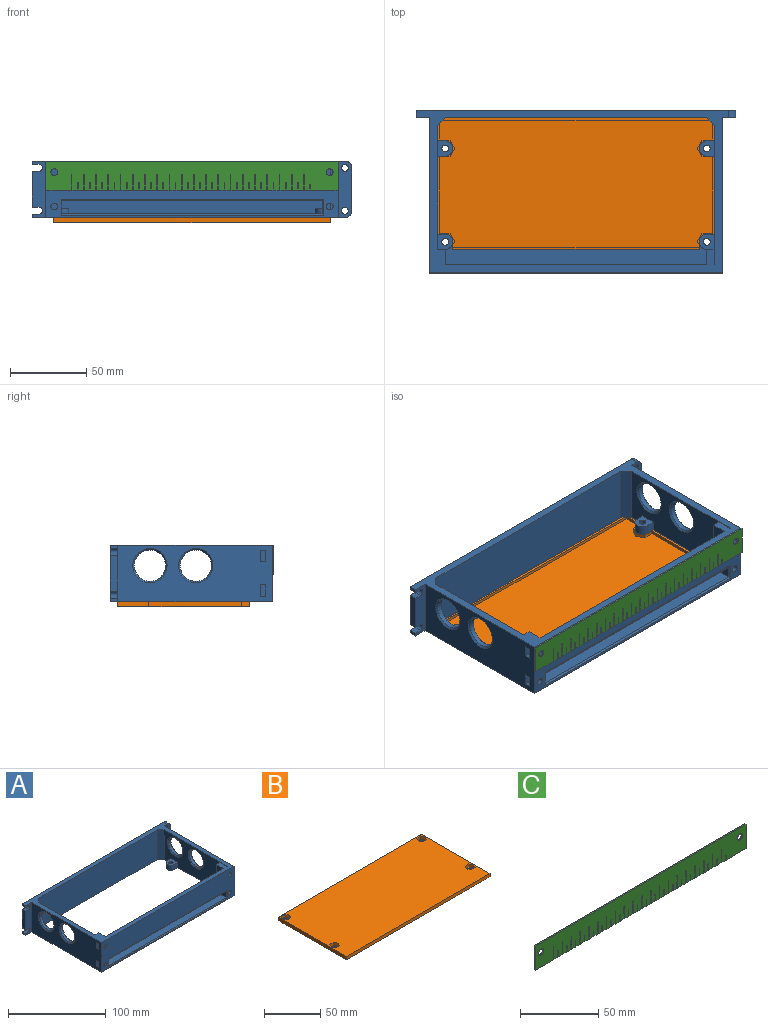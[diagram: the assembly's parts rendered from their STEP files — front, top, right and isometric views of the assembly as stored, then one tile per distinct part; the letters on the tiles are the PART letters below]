
ASSEMBLY  parts=3 mates=1
PART A: 147 faces, bbox 209x106x37 mm
  f0: cylinder r=1mm len=5mm, axis (0,-1,0), area 12.3mm2, adj f10,f16,f136,f145
  f1: plane 15.2x0.25mm, normal (0,1,0), area 3.8mm2, adj f11,f13,f123,f128
  f2: plane 1.1x0.25mm, normal (0,1,0), area 0.3mm2, adj f11,f13,f29,f129
  f3: cylinder r=2.25mm len=4.39mm, axis (0,-1,0), area 12.1mm2, adj f11,f71,f130
  f4: cylinder r=2.25mm len=4.5mm, axis (0,-1,0), area 63.6mm2, adj f10,f132
  f5: cylinder r=2.25mm len=4.39mm, axis (0,-1,0), area 12.1mm2, adj f11,f74,f124
  f6: cylinder r=2.25mm len=4.5mm, axis (0,-1,0), area 63.6mm2, adj f10,f125
  f7: plane 101x37mm, normal (-1,0,0), area 2890.7mm2, adj f9,f10,f23,f26,f108,f109,f110,f111
  f8: plane 171x37mm, normal (0,-1,0), area 6327mm2, adj f9,f26,f106,f107
  f9: plane 204.5x106mm, normal (0,0,-1), area 4958.2mm2, adj f7,f8,f10,f11,f14,f15,f18,f21
  f10: plane 191x37mm, normal (0,-1,0), area 5254mm2, adj f0,f4,f6,f7,f9,f14,f26,f27
  f11: plane 91x37mm, normal (-1,0,0), area 2361.4mm2, adj f1,f2,f3,f5,f9,f12,f26,f29
  f12: plane 3.6x0.25mm, normal (0,1,0), area 0.9mm2, adj f11,f13,f26,f122
  f13: plane 34.5x10mm, normal (1,0,0), area 283.3mm2, adj f1,f2,f12,f26,f29,f43,f57,f70
  f14: plane 101x37mm, normal (1,0,0), area 2890.7mm2, adj f9,f10,f18,f26,f122,f123,f124,f125
  f15: plane 81x37mm, normal (1,0,0), area 2077.8mm2, adj f9,f26,f33,f34,f35,f36,f38,f56
  f16: plane 170.5x26mm, normal (0,1,0), area 4432mm2, adj f0,f26,f27,f28,f30,f145
  f17: plane 170.5x18.99mm, normal (0,0,1), area 2397.7mm2, adj f22,f28,f30,f31,f44,f60,f62,f134
  f18: plane 37x9mm, normal (0,-1,0), area 292.5mm2, adj f9,f14,f24,f26,f51,f52,f64,f65
  f19: plane 23.5x5mm, normal (-1,0,0), area 117.5mm2, adj f21,f23,f50,f54
  f20: plane 5x2.25mm, normal (-1,0,0), area 11.2mm2, adj f21,f23,f26,f49
  f21: plane 209x37mm, normal (0,1,0), area 7636.1mm2, adj f9,f19,f20,f24,f25,f26,f48,f49
  f22: plane 161x2.5mm, normal (0,1,0), area 402.5mm2, adj f9,f17,f31,f44
  f23: plane 37x9mm, normal (0,-1,0), area 276.6mm2, adj f7,f9,f19,f20,f25,f26,f48,f49
  f24: plane 28x5mm, normal (1,0,0), area 140mm2, adj f18,f21,f64,f65
  f25: plane 5x2.25mm, normal (-1,0,0), area 11.3mm2, adj f9,f21,f23,f55
  f26: plane 204.5x106mm, normal (0,0,1), area 3065mm2, adj f7,f8,f10,f11,f12,f13,f14,f15
  f27: plane 170.5x5mm, normal (0,0,-1), area 852.5mm2, adj f10,f16,f28,f30,f146
  f28: plane 35.5x15mm, normal (1,0,0), area 388mm2, adj f10,f16,f17,f26,f27,f56,f60,f134
  f29: plane 10x0.25mm, normal (0,0,1), area 2.5mm2, adj f2,f11,f13,f43
  f30: plane 34.5x14mm, normal (-1,0,0), area 379mm2, adj f16,f17,f26,f27,f57,f62,f135
  f31: plane 6.2x5mm, normal (1,0,0), area 12.5mm2, adj f9,f17,f22,f34,f59,f60
  f32: cylinder r=2.25mm len=4.5mm, axis (0,0,-1), area 38.2mm2, adj f34,f98
  f33: plane 6.2x5mm, normal (0,1,0), area 31mm2, adj f9,f15,f34,f59
  f34: plane 10x10mm, normal (0,0,1), area 73.4mm2, adj f15,f31,f32,f33,f56,f59,f60
  f35: plane 6.2x5mm, normal (0,-1,0), area 31mm2, adj f9,f15,f38,f58
  f36: plane 6.2x5mm, normal (0,1,0), area 31mm2, adj f9,f15,f38,f58
  f37: cylinder r=2.25mm len=4.5mm, axis (0,0,-1), area 38.2mm2, adj f38,f91
  f38: plane 10x10mm, normal (0,0,1), area 73.4mm2, adj f15,f35,f36,f37,f58
  f39: plane 6.2x5mm, normal (0,1,0), area 31mm2, adj f9,f11,f42,f63
  f40: plane 6.2x5mm, normal (0,-1,0), area 31mm2, adj f9,f11,f42,f63
  f41: cylinder r=2.25mm len=4.5mm, axis (0,0,-1), area 38.2mm2, adj f42,f105
  f42: plane 10x10mm, normal (0,0,1), area 73.4mm2, adj f11,f39,f40,f41,f63
  f43: plane 3.7x0.25mm, normal (0,-1,0), area 0.9mm2, adj f11,f13,f29,f47
  f44: plane 6.2x5mm, normal (-1,0,0), area 12.5mm2, adj f9,f17,f22,f47,f61,f62
  f45: plane 6.2x5mm, normal (0,1,0), area 31mm2, adj f9,f11,f47,f61
  f46: cylinder r=2.25mm len=4.5mm, axis (0,0,-1), area 38.2mm2, adj f47,f84
  f47: plane 10x10mm, normal (0,0,1), area 73.4mm2, adj f11,f43,f44,f45,f46,f57,f61,f62
  f48: cylinder r=2.25mm len=5mm, axis (0,-1,0), area 35.3mm2, adj f21,f23,f49,f50
  f49: plane 5x4.5mm, normal (0,0,-1), area 22.5mm2, adj f20,f21,f23,f48
  f50: plane 5x4.5mm, normal (0,0,1), area 22.5mm2, adj f19,f21,f23,f48
  f51: cylinder r=2.25mm len=5mm, axis (0,-1,0), area 70.7mm2, adj f18,f21
  f52: cylinder r=2.25mm len=5mm, axis (0,-1,0), area 70.7mm2, adj f18,f21
  f53: cylinder r=2.25mm len=5mm, axis (0,-1,0), area 35.3mm2, adj f21,f23,f54,f55
  f54: plane 5x4.5mm, normal (0,0,-1), area 22.5mm2, adj f19,f21,f23,f53
  f55: plane 5x4.5mm, normal (0,0,1), area 22.5mm2, adj f21,f23,f25,f53
  f56: plane 30.8x5.25mm, normal (0,1,0), area 161.7mm2, adj f15,f26,f28,f34
  f57: plane 30.8x5mm, normal (0,1,0), area 154mm2, adj f13,f26,f30,f47
  f58: cylinder r=5mm len=10mm, axis (0,0,-1), area 97.4mm2, adj f9,f35,f36,f38
  f59: cylinder r=5mm len=6.2mm, axis (0,0,1), area 48.7mm2, adj f9,f31,f33,f34
  f60: cylinder r=5mm len=4.99mm, axis (0,0,1), area 28.1mm2, adj f17,f28,f31,f34
  f61: cylinder r=5mm len=6.2mm, axis (0,0,1), area 48.7mm2, adj f9,f44,f45,f47
  f62: cylinder r=5mm len=4.99mm, axis (0,0,1), area 28.1mm2, adj f17,f30,f44,f47
  f63: cylinder r=5mm len=10mm, axis (0,0,-1), area 97.4mm2, adj f9,f39,f40,f42
  f64: cylinder r=4.5mm len=5mm, axis (0,1,0), area 35.3mm2, adj f9,f18,f21,f24
  f65: cylinder r=4.5mm len=5mm, axis (0,-1,0), area 35.3mm2, adj f18,f21,f24,f26
  f66: cylinder r=10.25mm len=20.5mm, axis (1,0,0), area 193.2mm2, adj f142,f144
  f67: cylinder r=10.25mm len=20.5mm, axis (1,0,0), area 193.2mm2, adj f141,f143
  f68: cylinder r=10.25mm len=20.5mm, axis (1,0,0), area 193.2mm2, adj f137,f140
  f69: cylinder r=10.25mm len=20.5mm, axis (1,0,0), area 193.2mm2, adj f138,f139
  f70: cylinder r=2.25mm len=4.5mm, axis (0,-1,0), area 15.1mm2, adj f13,f72,f131
  f71: plane 4.39x1.75mm, normal (0,-1,0), area 5.7mm2, adj f3,f11
  f72: plane 4.5x2.5mm, normal (0,-1,0), area 9.1mm2, adj f13,f70
  f73: cylinder r=2.25mm len=4.5mm, axis (0,-1,0), area 15.1mm2, adj f13,f75,f126
  f74: plane 4.39x1.75mm, normal (0,-1,0), area 5.7mm2, adj f5,f11
  f75: plane 4.5x2.5mm, normal (0,-1,0), area 9.1mm2, adj f13,f73
  f76: cylinder r=2.25mm len=4.5mm, axis (0,-1,0), area 63.6mm2, adj f10,f118
  f77: cylinder r=2.25mm len=4.5mm, axis (0,-1,0), area 63.6mm2, adj f10,f109
  f78: plane 3.63x3.5mm, normal (-0.5,0.87,0), area 14.7mm2, adj f9,f79,f83,f84
  f79: plane 3.63x3.5mm, normal (0.5,0.87,0), area 14.7mm2, adj f9,f78,f80,f84
  f80: plane 4.19x3.5mm, normal (1,0,0), area 14.7mm2, adj f9,f79,f81,f84
  f81: plane 3.63x3.5mm, normal (0.5,-0.87,0), area 14.7mm2, adj f9,f80,f82,f84
  f82: plane 3.63x3.5mm, normal (-0.5,-0.87,0), area 14.7mm2, adj f9,f81,f83,f84
  f83: plane 4.19x3.5mm, normal (-1,0,0), area 14.7mm2, adj f9,f78,f82,f84
  f84: plane 8.37x7.25mm, normal (0,0,-1), area 29.6mm2, adj f46,f78,f79,f80,f81,f82,f83
  f85: plane 4.19x3.5mm, normal (0,-1,0), area 14.7mm2, adj f9,f86,f90,f91
  f86: plane 3.63x3.5mm, normal (-0.87,-0.5,0), area 14.7mm2, adj f9,f85,f87,f91
  f87: plane 3.63x3.5mm, normal (-0.87,0.5,0), area 14.7mm2, adj f9,f86,f88,f91
  f88: plane 4.19x3.5mm, normal (0,1,0), area 14.7mm2, adj f9,f87,f89,f91
  f89: plane 3.63x3.5mm, normal (0.87,0.5,0), area 14.7mm2, adj f9,f88,f90,f91
  f90: plane 3.63x3.5mm, normal (0.87,-0.5,0), area 14.7mm2, adj f9,f85,f89,f91
  f91: plane 8.37x7.25mm, normal (0,0,-1), area 29.6mm2, adj f37,f85,f86,f87,f88,f89,f90
  f92: plane 4.19x3.5mm, normal (0,-1,0), area 14.7mm2, adj f9,f93,f97,f98
  f93: plane 3.63x3.5mm, normal (-0.87,-0.5,0), area 14.7mm2, adj f9,f92,f94,f98
  f94: plane 3.63x3.5mm, normal (-0.87,0.5,0), area 14.7mm2, adj f9,f93,f95,f98
  f95: plane 4.19x3.5mm, normal (0,1,0), area 14.7mm2, adj f9,f94,f96,f98
  f96: plane 3.63x3.5mm, normal (0.87,0.5,0), area 14.7mm2, adj f9,f95,f97,f98
  f97: plane 3.63x3.5mm, normal (0.87,-0.5,0), area 14.7mm2, adj f9,f92,f96,f98
  f98: plane 8.37x7.25mm, normal (0,0,-1), area 29.6mm2, adj f32,f92,f93,f94,f95,f96,f97
  f99: plane 3.63x3.5mm, normal (-0.5,0.87,0), area 14.7mm2, adj f9,f100,f104,f105
  f100: plane 3.63x3.5mm, normal (0.5,0.87,0), area 14.7mm2, adj f9,f99,f101,f105
  f101: plane 4.19x3.5mm, normal (1,0,0), area 14.7mm2, adj f9,f100,f102,f105
  f102: plane 3.63x3.5mm, normal (0.5,-0.87,0), area 14.7mm2, adj f9,f101,f103,f105
  f103: plane 3.63x3.5mm, normal (-0.5,-0.87,0), area 14.7mm2, adj f9,f102,f104,f105
  f104: plane 4.19x3.5mm, normal (-1,0,0), area 14.7mm2, adj f9,f99,f103,f105
  f105: plane 8.37x7.25mm, normal (0,0,-1), area 29.6mm2, adj f41,f99,f100,f101,f102,f103,f104
  f106: plane 37x5mm, normal (0.71,-0.71,0), area 261.6mm2, adj f8,f9,f15,f26
  f107: plane 37x5mm, normal (-0.71,-0.71,0), area 261.6mm2, adj f8,f9,f11,f26
  f108: plane 9x7.3mm, normal (0,-1,0), area 49.8mm2, adj f7,f110,f111,f112,f114
  f109: plane 9x7.3mm, normal (0,1,0), area 49.8mm2, adj f7,f77,f110,f111,f112
  f110: plane 9x3.5mm, normal (0,0,-1), area 31.5mm2, adj f7,f108,f109,f112
  f111: plane 9x3.5mm, normal (0,0,1), area 31.5mm2, adj f7,f108,f109,f112
  f112: plane 7.3x3.5mm, normal (-1,0,0), area 25.6mm2, adj f108,f109,f110,f111
  f113: plane 4.5x4.5mm, normal (0,-1,0), area 15.9mm2, adj f114
  f114: cylinder r=2.25mm len=4.5mm, axis (0,-1,0), area 28.3mm2, adj f108,f113
  f115: plane 9x3.5mm, normal (0,0,-1), area 31.5mm2, adj f7,f116,f118,f119
  f116: plane 9x7.3mm, normal (0,-1,0), area 49.8mm2, adj f7,f115,f117,f119,f121
  f117: plane 9x3.5mm, normal (0,0,1), area 31.5mm2, adj f7,f116,f118,f119
  f118: plane 9x7.3mm, normal (0,1,0), area 49.8mm2, adj f7,f76,f115,f117,f119
  f119: plane 7.3x3.5mm, normal (-1,0,0), area 25.6mm2, adj f115,f116,f117,f118
  f120: plane 4.5x4.5mm, normal (0,-1,0), area 15.9mm2, adj f121
  f121: cylinder r=2.25mm len=4.5mm, axis (0,-1,0), area 28.3mm2, adj f116,f120
  f122: plane 9x3.5mm, normal (0,0,-1), area 30.8mm2, adj f11,f12,f13,f14,f124,f125,f126,f127
  f123: plane 9x3.5mm, normal (0,0,1), area 30.8mm2, adj f1,f11,f13,f14,f124,f125,f126,f127
  f124: plane 7.3x5mm, normal (0,-1,0), area 30.8mm2, adj f5,f11,f14,f122,f123
  f125: plane 9x7.3mm, normal (0,1,0), area 49.8mm2, adj f6,f14,f122,f123,f127
  f126: plane 7.3x3.75mm, normal (0,-1,0), area 18.3mm2, adj f13,f73,f122,f123,f127
  f127: plane 7.3x3.5mm, normal (1,0,0), area 25.6mm2, adj f122,f123,f125,f126
  f128: plane 9x3.5mm, normal (0,0,-1), area 30.8mm2, adj f1,f11,f13,f14,f130,f131,f132,f133
  f129: plane 9x3.5mm, normal (0,0,1), area 30.8mm2, adj f2,f11,f13,f14,f130,f131,f132,f133
  f130: plane 7.3x5mm, normal (0,-1,0), area 30.8mm2, adj f3,f11,f14,f128,f129
  f131: plane 7.3x3.75mm, normal (0,-1,0), area 18.3mm2, adj f13,f70,f128,f129,f133
  f132: plane 9x7.3mm, normal (0,1,0), area 49.8mm2, adj f4,f14,f128,f129,f133
  f133: plane 7.3x3.5mm, normal (1,0,0), area 25.6mm2, adj f128,f129,f131,f132
  f134: plane 171.5x1mm, normal (0,-0.71,0.71), area 241.8mm2, adj f10,f17,f28,f135
  f135: plane 10.5x1mm, normal (-0.71,-0.71,0), area 13.4mm2, adj f10,f30,f134,f136
  f136: plane 170.5x1mm, normal (0,-0.71,-0.71), area 167.8mm2, adj f0,f10,f135,f145,f146
  f137: cone r=11.25mm half-angle=45deg, axis (-1,0,0), area 95.5mm2, adj f11,f68
  f138: cone r=10.25mm half-angle=45deg, axis (-1,0,0), area 95.5mm2, adj f11,f69
  f139: cone r=11.25mm half-angle=45deg, axis (1,0,0), area 95.5mm2, adj f14,f69
  f140: cone r=10.25mm half-angle=45deg, axis (1,0,0), area 95.5mm2, adj f14,f68
  f141: cone r=11.25mm half-angle=45deg, axis (1,0,0), area 95.5mm2, adj f15,f67
  f142: cone r=10.25mm half-angle=45deg, axis (1,0,0), area 95.5mm2, adj f15,f66
  f143: cone r=10.25mm half-angle=45deg, axis (-1,0,0), area 95.5mm2, adj f7,f67
  f144: cone r=11.25mm half-angle=45deg, axis (-1,0,0), area 95.5mm2, adj f7,f66
  f145: plane 170.45x5mm, normal (0,0,1), area 127.5mm2, adj f0,f10,f16,f136,f146
  f146: plane 1x0.3mm, normal (1,0,0), area 0.3mm2, adj f10,f27,f136,f145
PART B: 73 faces, bbox 181x86x5 mm
  f0: plane 181x86mm, normal (0,0,-1), area 972mm2, adj f6,f7,f8,f9,f10,f12,f14,f16
  f1: plane 181x86mm, normal (0,0,1), area 15355.2mm2, adj f6,f7,f8,f9,f18,f19,f20,f21
  f2: cylinder r=2.25mm len=4.5mm, axis (0,0,1), area 25.4mm2, adj f11,f45
  f3: cylinder r=2.25mm len=4.5mm, axis (0,0,1), area 25.4mm2, adj f13,f38
  f4: cylinder r=2.25mm len=4.5mm, axis (0,0,1), area 25.4mm2, adj f15,f31
  f5: cylinder r=2.25mm len=4.5mm, axis (0,0,1), area 25.4mm2, adj f17,f24
  f6: plane 181x3.5mm, normal (0,-1,0), area 633.5mm2, adj f0,f1,f7,f9
  f7: plane 86x3.5mm, normal (1,0,0), area 301mm2, adj f0,f1,f6,f8
  f8: plane 181x3.5mm, normal (0,1,0), area 633.5mm2, adj f0,f1,f7,f9
  f9: plane 86x3.5mm, normal (-1,0,0), area 301mm2, adj f0,f1,f6,f8
  f10: cylinder r=3.4mm len=6.8mm, axis (0,0,1), area 32mm2, adj f0,f11
  f11: plane 6.8x6.8mm, normal (0,0,-1), area 20.4mm2, adj f2,f10
  f12: cylinder r=3.4mm len=6.8mm, axis (0,0,1), area 32mm2, adj f0,f13
  f13: plane 6.8x6.8mm, normal (0,0,-1), area 20.4mm2, adj f3,f12
  f14: cylinder r=3.4mm len=6.8mm, axis (0,0,1), area 32mm2, adj f0,f15
  f15: plane 6.8x6.8mm, normal (0,0,-1), area 20.4mm2, adj f4,f14
  f16: cylinder r=3.4mm len=6.8mm, axis (0,0,1), area 32mm2, adj f0,f17
  f17: plane 6.8x6.8mm, normal (0,0,-1), area 20.4mm2, adj f5,f16
  f18: plane 3.9x3.2mm, normal (0.87,-0.5,0), area 14.4mm2, adj f1,f19,f23,f24
  f19: plane 3.9x3.2mm, normal (0.87,0.5,0), area 14.4mm2, adj f1,f18,f20,f24
  f20: plane 4.5x3.2mm, normal (0,1,0), area 14.4mm2, adj f1,f19,f21,f24
  f21: plane 3.9x3.2mm, normal (-0.87,0.5,0), area 14.4mm2, adj f1,f20,f22,f24
  f22: plane 3.9x3.2mm, normal (-0.87,-0.5,0), area 14.4mm2, adj f1,f21,f23,f24
  f23: plane 4.5x3.2mm, normal (0,-1,0), area 14.4mm2, adj f1,f18,f22,f24
  f24: plane 9.01x7.8mm, normal (0,0,1), area 36.8mm2, adj f5,f18,f19,f20,f21,f22,f23
  f25: plane 3.9x3.2mm, normal (0.87,-0.5,0), area 14.4mm2, adj f1,f26,f30,f31
  f26: plane 3.9x3.2mm, normal (0.87,0.5,0), area 14.4mm2, adj f1,f25,f27,f31
  f27: plane 4.5x3.2mm, normal (0,1,0), area 14.4mm2, adj f1,f26,f28,f31
  f28: plane 3.9x3.2mm, normal (-0.87,0.5,0), area 14.4mm2, adj f1,f27,f29,f31
  f29: plane 3.9x3.2mm, normal (-0.87,-0.5,0), area 14.4mm2, adj f1,f28,f30,f31
  f30: plane 4.5x3.2mm, normal (0,-1,0), area 14.4mm2, adj f1,f25,f29,f31
  f31: plane 9.01x7.8mm, normal (0,0,1), area 36.8mm2, adj f4,f25,f26,f27,f28,f29,f30
  f32: plane 3.9x3.2mm, normal (0.87,-0.5,0), area 14.4mm2, adj f1,f33,f37,f38
  f33: plane 3.9x3.2mm, normal (0.87,0.5,0), area 14.4mm2, adj f1,f32,f34,f38
  f34: plane 4.5x3.2mm, normal (0,1,0), area 14.4mm2, adj f1,f33,f35,f38
  f35: plane 3.9x3.2mm, normal (-0.87,0.5,0), area 14.4mm2, adj f1,f34,f36,f38
  f36: plane 3.9x3.2mm, normal (-0.87,-0.5,0), area 14.4mm2, adj f1,f35,f37,f38
  f37: plane 4.5x3.2mm, normal (0,-1,0), area 14.4mm2, adj f1,f32,f36,f38
  f38: plane 9.01x7.8mm, normal (0,0,1), area 36.8mm2, adj f3,f32,f33,f34,f35,f36,f37
  f39: plane 4.5x3.2mm, normal (0,1,0), area 14.4mm2, adj f1,f40,f44,f45
  f40: plane 3.9x3.2mm, normal (-0.87,0.5,0), area 14.4mm2, adj f1,f39,f41,f45
  f41: plane 3.9x3.2mm, normal (-0.87,-0.5,0), area 14.4mm2, adj f1,f40,f42,f45
  f42: plane 4.5x3.2mm, normal (0,-1,0), area 14.4mm2, adj f1,f41,f43,f45
  f43: plane 3.9x3.2mm, normal (0.87,-0.5,0), area 14.4mm2, adj f1,f42,f44,f45
  f44: plane 3.9x3.2mm, normal (0.87,0.5,0), area 14.4mm2, adj f1,f39,f43,f45
  f45: plane 9.01x7.8mm, normal (0,0,1), area 36.8mm2, adj f2,f39,f40,f41,f42,f43,f44
  f46: plane 5.4x3.12mm, normal (0.87,0.5,0), area 12.5mm2, adj f0,f47,f52,f68
  f47: plane 5.4x3.12mm, normal (0.87,-0.5,0), area 12.5mm2, adj f0,f46,f48,f52
  f48: plane 6.24x2mm, normal (0,-1,0), area 12.5mm2, adj f0,f47,f49,f52
  f49: plane 2x0.66mm, normal (-0.87,-0.5,0), area 1.5mm2, adj f0,f48,f52,f56
  f50: plane 13.66x2mm, normal (-1,0,0), area 27.3mm2, adj f0,f52,f53,f60
  f51: plane 51.62x2mm, normal (1,0,0), area 103.2mm2, adj f0,f52,f67,f72
  f52: plane 178x83mm, normal (0,0,-1), area 14448.8mm2, adj f46,f47,f48,f49,f50,f51,f53,f54
  f53: plane 178x2mm, normal (0,1,0), area 356mm2, adj f0,f50,f52,f56
  f54: plane 51.62x2mm, normal (-1,0,0), area 103.2mm2, adj f0,f52,f61,f66
  f55: plane 162.57x2mm, normal (0,-1,0), area 325.1mm2, adj f0,f52,f63,f71
  f56: plane 13.66x2mm, normal (1,0,0), area 27.3mm2, adj f0,f49,f52,f53
  f57: plane 5.4x3.12mm, normal (-0.87,0.5,0), area 12.5mm2, adj f0,f52,f58,f62
  f58: plane 5.4x3.12mm, normal (-0.87,-0.5,0), area 12.5mm2, adj f0,f52,f57,f59
  f59: plane 6.24x2mm, normal (0,-1,0), area 12.5mm2, adj f0,f52,f58,f60
  f60: plane 2x0.66mm, normal (0.87,-0.5,0), area 1.5mm2, adj f0,f50,f52,f59
  f61: plane 2x0.66mm, normal (0.87,0.5,0), area 1.5mm2, adj f0,f52,f54,f62
  f62: plane 6.24x2mm, normal (0,1,0), area 12.5mm2, adj f0,f52,f57,f61
  f63: plane 3.5x2.02mm, normal (-0.87,0.5,0), area 8.1mm2, adj f0,f52,f55,f64
  f64: plane 5.4x3.12mm, normal (-0.87,-0.5,0), area 12.5mm2, adj f0,f52,f63,f65
  f65: plane 6.24x2mm, normal (0,-1,0), area 12.5mm2, adj f0,f52,f64,f66
  f66: plane 2x0.66mm, normal (0.87,-0.5,0), area 1.5mm2, adj f0,f52,f54,f65
  f67: plane 2x0.66mm, normal (-0.87,0.5,0), area 1.5mm2, adj f0,f51,f52,f68
  f68: plane 6.24x2mm, normal (0,1,0), area 12.5mm2, adj f0,f46,f52,f67
  f69: plane 6.24x2mm, normal (0,-1,0), area 12.5mm2, adj f0,f52,f70,f72
  f70: plane 5.4x3.12mm, normal (0.87,-0.5,0), area 12.5mm2, adj f0,f52,f69,f71
  f71: plane 3.5x2.02mm, normal (0.87,0.5,0), area 8.1mm2, adj f0,f52,f55,f70
  f72: plane 2x0.66mm, normal (-0.87,-0.5,0), area 1.5mm2, adj f0,f51,f52,f69
PART C: 170 faces, bbox 191x1x19 mm
  f0: plane 3.5x1mm, normal (0,0,-1), area 3.5mm2, adj f40,f41,f48,f168
  f1: plane 3.5x1mm, normal (0,0,-1), area 3.5mm2, adj f40,f41,f165,f167
  f2: plane 3.5x1mm, normal (0,0,-1), area 3.5mm2, adj f40,f41,f162,f164
  f3: plane 3.5x1mm, normal (0,0,-1), area 3.5mm2, adj f40,f41,f159,f161
  f4: plane 3.5x1mm, normal (0,0,-1), area 3.5mm2, adj f40,f41,f156,f158
  f5: plane 3.5x1mm, normal (0,0,-1), area 3.5mm2, adj f40,f41,f153,f155
  f6: plane 3.5x1mm, normal (0,0,-1), area 3.5mm2, adj f40,f41,f150,f152
  f7: plane 3.5x1mm, normal (0,0,-1), area 3.5mm2, adj f40,f41,f147,f149
  f8: plane 3.5x1mm, normal (0,0,-1), area 3.5mm2, adj f40,f41,f144,f146
  f9: plane 3.5x1mm, normal (0,0,-1), area 3.5mm2, adj f40,f41,f141,f143
  f10: plane 3.5x1mm, normal (0,0,-1), area 3.5mm2, adj f40,f41,f138,f140
  f11: plane 3.5x1mm, normal (0,0,-1), area 3.5mm2, adj f40,f41,f135,f137
  f12: plane 3.5x1mm, normal (0,0,-1), area 3.5mm2, adj f40,f41,f132,f134
  f13: plane 3.5x1mm, normal (0,0,-1), area 3.5mm2, adj f40,f41,f129,f131
  f14: plane 3.5x1mm, normal (0,0,-1), area 3.5mm2, adj f40,f41,f126,f128
  f15: plane 3.5x1mm, normal (0,0,-1), area 3.5mm2, adj f40,f41,f123,f125
  f16: plane 3.5x1mm, normal (0,0,-1), area 3.5mm2, adj f40,f41,f120,f122
  f17: plane 3.5x1mm, normal (0,0,-1), area 3.5mm2, adj f40,f41,f117,f119
  f18: plane 3.5x1mm, normal (0,0,-1), area 3.5mm2, adj f40,f41,f114,f116
  f19: plane 3.5x1mm, normal (0,0,-1), area 3.5mm2, adj f40,f41,f111,f113
  f20: plane 3.5x1mm, normal (0,0,-1), area 3.5mm2, adj f40,f41,f108,f110
  f21: plane 3.5x1mm, normal (0,0,-1), area 3.5mm2, adj f40,f41,f105,f107
  f22: plane 3.5x1mm, normal (0,0,-1), area 3.5mm2, adj f40,f41,f102,f104
  f23: plane 3.5x1mm, normal (0,0,-1), area 3.5mm2, adj f40,f41,f99,f101
  f24: plane 3.5x1mm, normal (0,0,-1), area 3.5mm2, adj f40,f41,f96,f98
  f25: plane 3.5x1mm, normal (0,0,-1), area 3.5mm2, adj f40,f41,f93,f95
  f26: plane 3.5x1mm, normal (0,0,-1), area 3.5mm2, adj f40,f41,f90,f92
  f27: plane 3.5x1mm, normal (0,0,-1), area 3.5mm2, adj f40,f41,f87,f89
  f28: plane 3.5x1mm, normal (0,0,-1), area 3.5mm2, adj f40,f41,f84,f86
  f29: plane 3.5x1mm, normal (0,0,-1), area 3.5mm2, adj f40,f41,f81,f83
  f30: plane 3.5x1mm, normal (0,0,-1), area 3.5mm2, adj f40,f41,f78,f80
  f31: plane 3.5x1mm, normal (0,0,-1), area 3.5mm2, adj f40,f41,f75,f77
  f32: plane 18x1mm, normal (0,0,-1), area 18mm2, adj f40,f41,f44,f72
  f33: plane 3.5x1mm, normal (0,0,-1), area 3.5mm2, adj f40,f41,f63,f67
  f34: plane 3.5x1mm, normal (0,0,-1), area 3.5mm2, adj f40,f41,f60,f64
  f35: plane 3.5x1mm, normal (0,0,-1), area 3.5mm2, adj f40,f41,f57,f61
  f36: plane 3.5x1mm, normal (0,0,-1), area 3.5mm2, adj f40,f41,f54,f58
  f37: plane 3.5x1mm, normal (0,0,-1), area 3.5mm2, adj f40,f41,f51,f55
  f38: plane 3.5x1mm, normal (0,0,-1), area 3.5mm2, adj f40,f41,f52,f74
  f39: plane 3.5x1mm, normal (0,0,-1), area 3.5mm2, adj f40,f41,f49,f70
  f40: plane 191x19mm, normal (0,-1,0), area 3447.9mm2, adj f0,f1,f2,f3,f4,f5,f6,f7
  f41: plane 191x19mm, normal (0,1,0), area 3447.9mm2, adj f0,f1,f2,f3,f4,f5,f6,f7
  f42: plane 19x1mm, normal (-1,0,0), area 19mm2, adj f40,f41,f43,f47
  f43: plane 16.5x1mm, normal (0,0,-1), area 16.5mm2, adj f40,f41,f42,f66
  f44: plane 19x1mm, normal (1,0,0), area 19mm2, adj f32,f40,f41,f47
  f45: cylinder r=2.25mm len=4.5mm, axis (0,1,0), area 14.1mm2, adj f40,f41
  f46: cylinder r=2.25mm len=4.5mm, axis (0,1,0), area 14.1mm2, adj f40,f41
  f47: plane 191x1mm, normal (0,0,1), area 191mm2, adj f40,f41,f42,f44
  f48: plane 10x1mm, normal (1,0,0), area 10mm2, adj f0,f40,f41,f50
  f49: plane 10x1mm, normal (-1,0,0), area 10mm2, adj f39,f40,f41,f50
  f50: plane 1x0.5mm, normal (0,0,-1), area 0.5mm2, adj f40,f41,f48,f49
  f51: plane 5x1mm, normal (1,0,0), area 5mm2, adj f37,f40,f41,f53
  f52: plane 5x1mm, normal (-1,0,0), area 5mm2, adj f38,f40,f41,f53
  f53: plane 1x0.5mm, normal (0,0,-1), area 0.5mm2, adj f40,f41,f51,f52
  f54: plane 10x1mm, normal (1,0,0), area 10mm2, adj f36,f40,f41,f56
  f55: plane 10x1mm, normal (-1,0,0), area 10mm2, adj f37,f40,f41,f56
  f56: plane 1x0.5mm, normal (0,0,-1), area 0.5mm2, adj f40,f41,f54,f55
  f57: plane 5x1mm, normal (1,0,0), area 5mm2, adj f35,f40,f41,f59
  f58: plane 5x1mm, normal (-1,0,0), area 5mm2, adj f36,f40,f41,f59
  f59: plane 1x0.5mm, normal (0,0,-1), area 0.5mm2, adj f40,f41,f57,f58
  f60: plane 10x1mm, normal (1,0,0), area 10mm2, adj f34,f40,f41,f62
  f61: plane 10x1mm, normal (-1,0,0), area 10mm2, adj f35,f40,f41,f62
  f62: plane 1x0.5mm, normal (0,0,-1), area 0.5mm2, adj f40,f41,f60,f61
  f63: plane 5x1mm, normal (1,0,0), area 5mm2, adj f33,f40,f41,f65
  f64: plane 5x1mm, normal (-1,0,0), area 5mm2, adj f34,f40,f41,f65
  f65: plane 1x0.5mm, normal (0,0,-1), area 0.5mm2, adj f40,f41,f63,f64
  f66: plane 10x1mm, normal (1,0,0), area 10mm2, adj f40,f41,f43,f68
  f67: plane 10x1mm, normal (-1,0,0), area 10mm2, adj f33,f40,f41,f68
  f68: plane 1x0.5mm, normal (0,0,-1), area 0.5mm2, adj f40,f41,f66,f67
  f69: plane 1x0.44mm, normal (-0.17,0,-0.98), area 0.4mm2, adj f40,f41,f70,f71
  f70: plane 3.6x1mm, normal (1,0,0), area 3.6mm2, adj f39,f40,f41,f69
  f71: plane 1x0.48mm, normal (-1,0,0), area 0.5mm2, adj f40,f41,f69,f73
  f72: plane 3.04x1mm, normal (-1,0,0), area 3mm2, adj f32,f40,f41,f73
  f73: plane 1x0.06mm, normal (0,0,-1), area 0.1mm2, adj f40,f41,f71,f72
  f74: plane 10x1mm, normal (1,0,0), area 10mm2, adj f38,f40,f41,f76
  f75: plane 10x1mm, normal (-1,0,0), area 10mm2, adj f31,f40,f41,f76
  f76: plane 1x0.5mm, normal (0,0,-1), area 0.5mm2, adj f40,f41,f74,f75
  f77: plane 5x1mm, normal (1,0,0), area 5mm2, adj f31,f40,f41,f79
  f78: plane 5x1mm, normal (-1,0,0), area 5mm2, adj f30,f40,f41,f79
  f79: plane 1x0.5mm, normal (0,0,-1), area 0.5mm2, adj f40,f41,f77,f78
  f80: plane 10x1mm, normal (1,0,0), area 10mm2, adj f30,f40,f41,f82
  f81: plane 10x1mm, normal (-1,0,0), area 10mm2, adj f29,f40,f41,f82
  f82: plane 1x0.5mm, normal (0,0,-1), area 0.5mm2, adj f40,f41,f80,f81
  f83: plane 5x1mm, normal (1,0,0), area 5mm2, adj f29,f40,f41,f85
  f84: plane 5x1mm, normal (-1,0,0), area 5mm2, adj f28,f40,f41,f85
  f85: plane 1x0.5mm, normal (0,0,-1), area 0.5mm2, adj f40,f41,f83,f84
  f86: plane 10x1mm, normal (1,0,0), area 10mm2, adj f28,f40,f41,f88
  f87: plane 10x1mm, normal (-1,0,0), area 10mm2, adj f27,f40,f41,f88
  f88: plane 1x0.5mm, normal (0,0,-1), area 0.5mm2, adj f40,f41,f86,f87
  f89: plane 5x1mm, normal (1,0,0), area 5mm2, adj f27,f40,f41,f91
  f90: plane 5x1mm, normal (-1,0,0), area 5mm2, adj f26,f40,f41,f91
  f91: plane 1x0.5mm, normal (0,0,-1), area 0.5mm2, adj f40,f41,f89,f90
  f92: plane 10x1mm, normal (1,0,0), area 10mm2, adj f26,f40,f41,f94
  f93: plane 10x1mm, normal (-1,0,0), area 10mm2, adj f25,f40,f41,f94
  f94: plane 1x0.5mm, normal (0,0,-1), area 0.5mm2, adj f40,f41,f92,f93
  f95: plane 5x1mm, normal (1,0,0), area 5mm2, adj f25,f40,f41,f97
  f96: plane 5x1mm, normal (-1,0,0), area 5mm2, adj f24,f40,f41,f97
  f97: plane 1x0.5mm, normal (0,0,-1), area 0.5mm2, adj f40,f41,f95,f96
  f98: plane 10x1mm, normal (1,0,0), area 10mm2, adj f24,f40,f41,f100
  f99: plane 10x1mm, normal (-1,0,0), area 10mm2, adj f23,f40,f41,f100
  f100: plane 1x0.5mm, normal (0,0,-1), area 0.5mm2, adj f40,f41,f98,f99
  f101: plane 5x1mm, normal (1,0,0), area 5mm2, adj f23,f40,f41,f103
  f102: plane 5x1mm, normal (-1,0,0), area 5mm2, adj f22,f40,f41,f103
  f103: plane 1x0.5mm, normal (0,0,-1), area 0.5mm2, adj f40,f41,f101,f102
  f104: plane 10x1mm, normal (1,0,0), area 10mm2, adj f22,f40,f41,f106
  f105: plane 10x1mm, normal (-1,0,0), area 10mm2, adj f21,f40,f41,f106
  f106: plane 1x0.5mm, normal (0,0,-1), area 0.5mm2, adj f40,f41,f104,f105
  f107: plane 5x1mm, normal (1,0,0), area 5mm2, adj f21,f40,f41,f109
  f108: plane 5x1mm, normal (-1,0,0), area 5mm2, adj f20,f40,f41,f109
  f109: plane 1x0.5mm, normal (0,0,-1), area 0.5mm2, adj f40,f41,f107,f108
  f110: plane 10x1mm, normal (1,0,0), area 10mm2, adj f20,f40,f41,f112
  f111: plane 10x1mm, normal (-1,0,0), area 10mm2, adj f19,f40,f41,f112
  f112: plane 1x0.5mm, normal (0,0,-1), area 0.5mm2, adj f40,f41,f110,f111
  f113: plane 5x1mm, normal (1,0,0), area 5mm2, adj f19,f40,f41,f115
  f114: plane 5x1mm, normal (-1,0,0), area 5mm2, adj f18,f40,f41,f115
  f115: plane 1x0.5mm, normal (0,0,-1), area 0.5mm2, adj f40,f41,f113,f114
  f116: plane 10x1mm, normal (1,0,0), area 10mm2, adj f18,f40,f41,f118
  f117: plane 10x1mm, normal (-1,0,0), area 10mm2, adj f17,f40,f41,f118
  f118: plane 1x0.5mm, normal (0,0,-1), area 0.5mm2, adj f40,f41,f116,f117
  f119: plane 5x1mm, normal (1,0,0), area 5mm2, adj f17,f40,f41,f121
  f120: plane 5x1mm, normal (-1,0,0), area 5mm2, adj f16,f40,f41,f121
  f121: plane 1x0.5mm, normal (0,0,-1), area 0.5mm2, adj f40,f41,f119,f120
  f122: plane 10x1mm, normal (1,0,0), area 10mm2, adj f16,f40,f41,f124
  f123: plane 10x1mm, normal (-1,0,0), area 10mm2, adj f15,f40,f41,f124
  f124: plane 1x0.5mm, normal (0,0,-1), area 0.5mm2, adj f40,f41,f122,f123
  f125: plane 5x1mm, normal (1,0,0), area 5mm2, adj f15,f40,f41,f127
  f126: plane 5x1mm, normal (-1,0,0), area 5mm2, adj f14,f40,f41,f127
  f127: plane 1x0.5mm, normal (0,0,-1), area 0.5mm2, adj f40,f41,f125,f126
  f128: plane 10x1mm, normal (1,0,0), area 10mm2, adj f14,f40,f41,f130
  f129: plane 10x1mm, normal (-1,0,0), area 10mm2, adj f13,f40,f41,f130
  f130: plane 1x0.5mm, normal (0,0,-1), area 0.5mm2, adj f40,f41,f128,f129
  f131: plane 5x1mm, normal (1,0,0), area 5mm2, adj f13,f40,f41,f133
  f132: plane 5x1mm, normal (-1,0,0), area 5mm2, adj f12,f40,f41,f133
  f133: plane 1x0.5mm, normal (0,0,-1), area 0.5mm2, adj f40,f41,f131,f132
  f134: plane 10x1mm, normal (1,0,0), area 10mm2, adj f12,f40,f41,f136
  f135: plane 10x1mm, normal (-1,0,0), area 10mm2, adj f11,f40,f41,f136
  f136: plane 1x0.5mm, normal (0,0,-1), area 0.5mm2, adj f40,f41,f134,f135
  f137: plane 5x1mm, normal (1,0,0), area 5mm2, adj f11,f40,f41,f139
  f138: plane 5x1mm, normal (-1,0,0), area 5mm2, adj f10,f40,f41,f139
  f139: plane 1x0.5mm, normal (0,0,-1), area 0.5mm2, adj f40,f41,f137,f138
  f140: plane 10x1mm, normal (1,0,0), area 10mm2, adj f10,f40,f41,f142
  f141: plane 10x1mm, normal (-1,0,0), area 10mm2, adj f9,f40,f41,f142
  f142: plane 1x0.5mm, normal (0,0,-1), area 0.5mm2, adj f40,f41,f140,f141
  f143: plane 5x1mm, normal (1,0,0), area 5mm2, adj f9,f40,f41,f145
  f144: plane 5x1mm, normal (-1,0,0), area 5mm2, adj f8,f40,f41,f145
  f145: plane 1x0.5mm, normal (0,0,-1), area 0.5mm2, adj f40,f41,f143,f144
  f146: plane 10x1mm, normal (1,0,0), area 10mm2, adj f8,f40,f41,f148
  f147: plane 10x1mm, normal (-1,0,0), area 10mm2, adj f7,f40,f41,f148
  f148: plane 1x0.5mm, normal (0,0,-1), area 0.5mm2, adj f40,f41,f146,f147
  f149: plane 5x1mm, normal (1,0,0), area 5mm2, adj f7,f40,f41,f151
  f150: plane 5x1mm, normal (-1,0,0), area 5mm2, adj f6,f40,f41,f151
  f151: plane 1x0.5mm, normal (0,0,-1), area 0.5mm2, adj f40,f41,f149,f150
  f152: plane 10x1mm, normal (1,0,0), area 10mm2, adj f6,f40,f41,f154
  f153: plane 10x1mm, normal (-1,0,0), area 10mm2, adj f5,f40,f41,f154
  f154: plane 1x0.5mm, normal (0,0,-1), area 0.5mm2, adj f40,f41,f152,f153
  f155: plane 5x1mm, normal (1,0,0), area 5mm2, adj f5,f40,f41,f157
  f156: plane 5x1mm, normal (-1,0,0), area 5mm2, adj f4,f40,f41,f157
  f157: plane 1x0.5mm, normal (0,0,-1), area 0.5mm2, adj f40,f41,f155,f156
  f158: plane 10x1mm, normal (1,0,0), area 10mm2, adj f4,f40,f41,f160
  f159: plane 10x1mm, normal (-1,0,0), area 10mm2, adj f3,f40,f41,f160
  f160: plane 1x0.5mm, normal (0,0,-1), area 0.5mm2, adj f40,f41,f158,f159
  f161: plane 5x1mm, normal (1,0,0), area 5mm2, adj f3,f40,f41,f163
  f162: plane 5x1mm, normal (-1,0,0), area 5mm2, adj f2,f40,f41,f163
  f163: plane 1x0.5mm, normal (0,0,-1), area 0.5mm2, adj f40,f41,f161,f162
  f164: plane 10x1mm, normal (1,0,0), area 10mm2, adj f2,f40,f41,f166
  f165: plane 10x1mm, normal (-1,0,0), area 10mm2, adj f1,f40,f41,f166
  f166: plane 1x0.5mm, normal (0,0,-1), area 0.5mm2, adj f40,f41,f164,f165
  f167: plane 5x1mm, normal (1,0,0), area 5mm2, adj f1,f40,f41,f169
  f168: plane 5x1mm, normal (-1,0,0), area 5mm2, adj f0,f40,f41,f169
  f169: plane 1x0.5mm, normal (0,0,-1), area 0.5mm2, adj f40,f41,f167,f168
PLACE A at identity
PLACE B rot(axis=(1,0,0),180deg) t=(0,5,0)mm
PLACE C at identity
MATE cylindrical B.f4 <-> A.f46  axis (0,0,1) through (85.5,-33,0)mm
